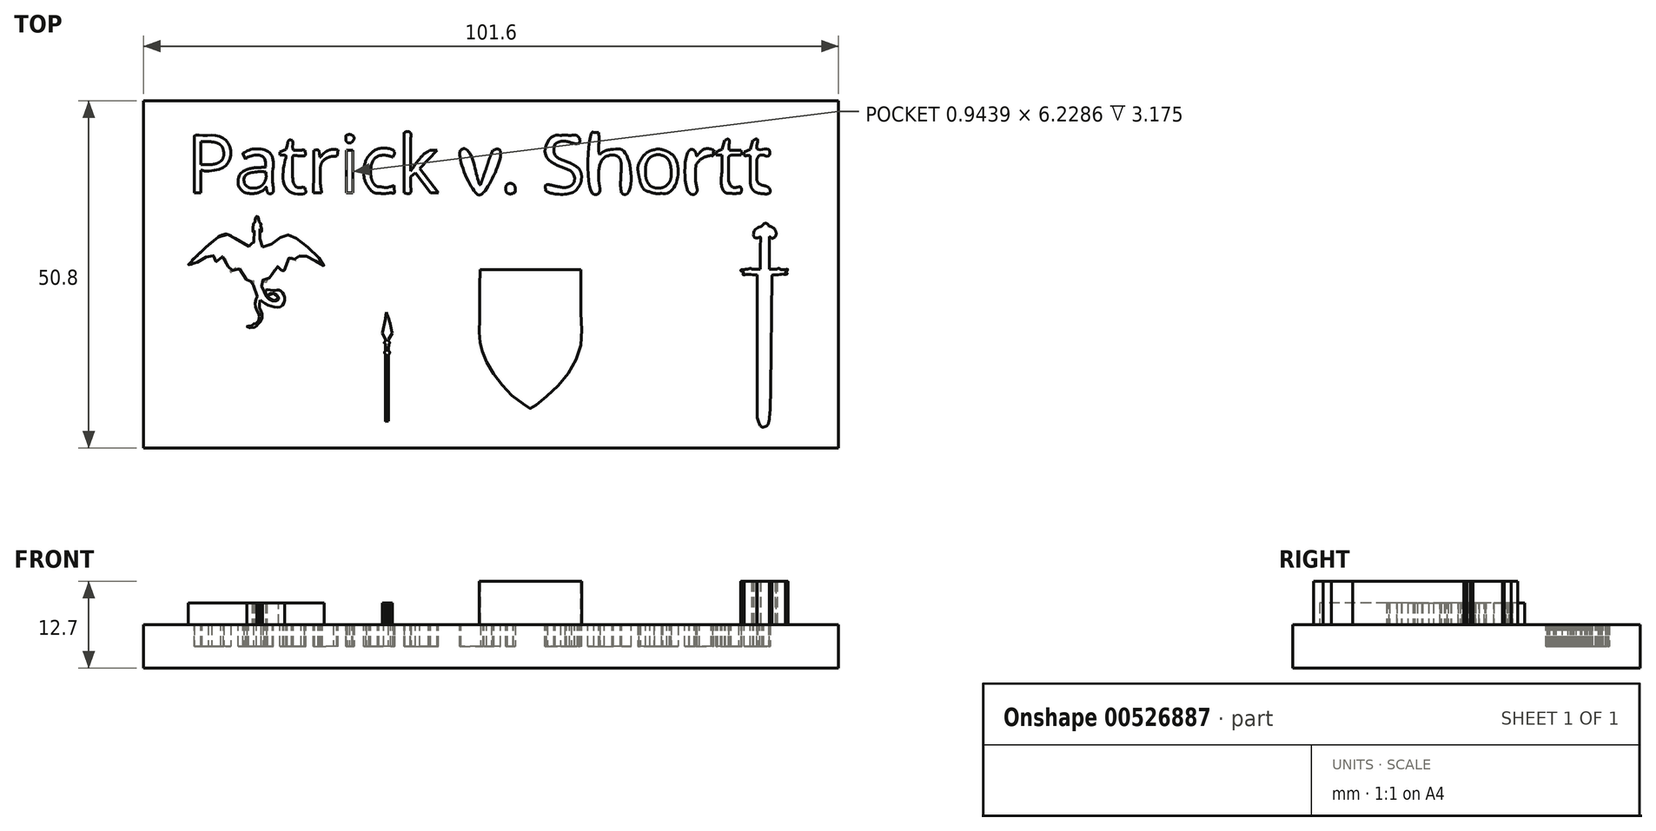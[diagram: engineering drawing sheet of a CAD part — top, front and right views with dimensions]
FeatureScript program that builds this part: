
annotation { "Feature Type Name" : "Feature", "Feature Type Description" : "" }
export const myFeature = defineFeature(function(context is Context, id is Id, definition is map)
    precondition{}
    {
        {
            var Q0;
            Q0=qCreatedBy(makeId("Top.planeOp"),FACE);
            var sketch = newSketch(context, id + "F0", { "sketchPlane" : qUnion([Q0])});
            skLineSegment(sketch, "E0.bottom", {"start": v(-59.4, 0) * mm, "end": v(42.2, 0) * mm});
            skLineSegment(sketch, "E0.top", {"start": v(-59.4, 50.8) * mm, "end": v(42.2, 50.8) * mm});
            skLineSegment(sketch, "E0.left", {"start": v(-59.4, 0) * mm, "end": v(-59.4, 50.8) * mm});
            skLineSegment(sketch, "E0.right", {"start": v(42.2, 0) * mm, "end": v(42.2, 50.8) * mm});
            skSolve(sketch);
        }
        {
            var Q0;
            Q0=makeQuery(id+"F0.imprint","IMPRINT",FACE,{"disambiguationData":[TD([[makeQuery(id+"F0.imprint","IMPRINT",EDGE,{"derivedFrom":sQuery(id+"F0.wireOp",EDGE,"E0.bottom")}),1.0]])]});
            extrude(context, id + "F1", {"entities" : qUnion([Q0]), "depth" : 6.35 * mm, "offsetDistance" : 25.4 * mm});
        }
        {
            var Q0;
            Q0=makeQuery(id+"F1.opExtrude","CAP_FACE",FACE,{"disambiguationData":[OSD([sQuery(id+"F0.wireOp",EDGE,"E0.bottom"),sQuery(id+"F0.wireOp",EDGE,"E0.top"),sQuery(id+"F0.wireOp",EDGE,"E0.left"),sQuery(id+"F0.wireOp",EDGE,"E0.right")])],"isStart":false});
            var sketch = newSketch(context, id + "F2", { "sketchPlane" : qUnion([Q0])});
            skText(sketch, "E1", { "text": "Patrick v. Shortt\n", "fontName": "OpenSans-Regular.ttf"});
            skFitSpline(sketch, "E2", {"points": [v(-51.95, 37.34) * mm, v(-51.93, 38.16) * mm, v(-51.93, 38.92) * mm, v(-51.96, 39.37) * mm, v(-51.93, 43.02) * mm, v(-51.93, 45.24) * mm, v(-51.93, 45.72) * mm, v(-50.8, 45.72) * mm, v(-48.78, 45.72) * mm, v(-47.31, 44.97) * mm, v(-46.64, 43.43) * mm, v(-47.09, 41.63) * mm, v(-48.59, 40.73) * mm, v(-50.77, 40.58) * mm, v(-51.03, 40.65) * mm, v(-50.96, 37.34) * mm], "startDerivative": vector(0.26, 16.03) * mm, "endDerivative": vector(3.57, -47.2) * mm});
            skFitSpline(sketch, "E3", {"points": [v(-51, 44.75) * mm, v(-51, 41.63) * mm], "startDerivative": vector(0, -3.12) * mm, "endDerivative": vector(0, -3.12) * mm});
            skFitSpline(sketch, "E4", {"points": [v(-51, 41.63) * mm, v(-49.11, 41.63) * mm, v(-47.84, 42.27) * mm, v(-47.76, 43.7) * mm, v(-48.33, 44.41) * mm, v(-49.38, 44.79) * mm, v(-50.43, 44.79) * mm, v(-51, 44.75) * mm], "startDerivative": vector(10.5, -0.7) * mm, "endDerivative": vector(-5.2, -0.33) * mm});
            skFitSpline(sketch, "E5", {"points": [v(-44.83, 43.06) * mm, v(-44.5, 42.23) * mm], "startDerivative": vector(0.34, -0.83) * mm, "endDerivative": vector(0.34, -0.83) * mm});
            skFitSpline(sketch, "E6", {"points": [v(-44.5, 42.23) * mm, v(-44.23, 42.5) * mm, v(-43.4, 42.79) * mm, v(-42.54, 42.85) * mm, v(-41.94, 42.62) * mm, v(-41.64, 42.14) * mm, v(-41.51, 41.11) * mm, v(-41.52, 41.07) * mm, v(-41.76, 41.06) * mm, v(-42.17, 41.05) * mm, v(-42.72, 41.03) * mm, v(-43.11, 41) * mm, v(-43.71, 40.9) * mm, v(-44.38, 40.71) * mm, v(-45.03, 40.32) * mm, v(-45.5, 39.57) * mm, v(-45.54, 38.58) * mm, v(-45.3, 38) * mm, v(-44.5, 37.34) * mm, v(-43.22, 37.34) * mm, v(-41.77, 37.8) * mm, v(-41.46, 38.2) * mm, v(-41.21, 37.34) * mm, v(-40.51, 37.34) * mm, v(-40.56, 39.3) * mm, v(-40.41, 41.85) * mm, v(-40.96, 43.2) * mm, v(-42.37, 43.76) * mm, v(-43.87, 43.6) * mm, v(-44.83, 43.06) * mm], "startDerivative": vector(8.8, 12.46) * mm, "endDerivative": vector(-22.31, -15.8) * mm});
            skFitSpline(sketch, "E7", {"points": [v(-41.67, 40.35) * mm, v(-42.92, 40.4) * mm, v(-44.5, 39.85) * mm, v(-44.5, 38.5) * mm, v(-43.02, 38.1) * mm, v(-41.92, 38.7) * mm, v(-41.46, 39.55) * mm, v(-41.67, 40.35) * mm]});
            skFitSpline(sketch, "E8", {"points": [v(-38.15, 45.01) * mm, v(-38.56, 43.66) * mm, v(-39.3, 43.26) * mm, v(-39.36, 42.9) * mm, v(-38.6, 42.8) * mm, v(-38.66, 42.2) * mm, v(-38.4, 37.84) * mm, v(-35.7, 37.34) * mm, v(-35.8, 37.9) * mm, v(-36, 38.14) * mm, v(-36.75, 38.1) * mm, v(-37.3, 38.44) * mm, v(-37.55, 39.3) * mm, v(-37.55, 42.66) * mm, v(-37.3, 42.8) * mm, v(-35.8, 42.8) * mm, v(-35.8, 43.4) * mm, v(-36.05, 43.6) * mm, v(-37.4, 43.5) * mm, v(-37.55, 44.56) * mm, v(-37.65, 44.96) * mm, v(-38.15, 45.01) * mm]});
            skFitSpline(sketch, "E9", {"points": [v(-34.4, 43.56) * mm, v(-34.6, 37.34) * mm], "startDerivative": vector(-0.2, -6.22) * mm, "endDerivative": vector(-0.2, -6.22) * mm});
            skFitSpline(sketch, "E10", {"points": [v(-34.6, 37.34) * mm, v(-33.34, 37.34) * mm], "startDerivative": vector(1.25, 0) * mm, "endDerivative": vector(1.25, 0) * mm});
            skFitSpline(sketch, "E11", {"points": [v(-34.4, 43.56) * mm, v(-33.84, 43.56) * mm, v(-33.8, 42.5) * mm, v(-32.79, 43.16) * mm, v(-31.84, 43.56) * mm, v(-31.23, 43.56) * mm, v(-31.08, 42.8) * mm, v(-31.84, 42.66) * mm, v(-33.34, 41.75) * mm, v(-33.34, 37.34) * mm], "startDerivative": vector(9.35, 3.26) * mm, "endDerivative": vector(3.7, -24.46) * mm});
            skFitSpline(sketch, "E12", {"points": [v(-29.48, 44.86) * mm, v(-29.73, 45.01) * mm, v(-29.78, 45.72) * mm, v(-29.33, 45.72) * mm, v(-28.78, 45.72) * mm, v(-28.68, 45.06) * mm, v(-29.48, 44.86) * mm]});
            skFitSpline(sketch, "E13", {"points": [v(-29.73, 43.4) * mm, v(-29.78, 37.34) * mm], "startDerivative": vector(-0.05, -6.07) * mm, "endDerivative": vector(-0.05, -6.07) * mm});
            skFitSpline(sketch, "E14", {"points": [v(-29.78, 37.34) * mm, v(-28.68, 37.34) * mm], "startDerivative": vector(1.1, 0) * mm, "endDerivative": vector(1.1, 0) * mm});
            skFitSpline(sketch, "E15", {"points": [v(-28.68, 37.34) * mm, v(-28.68, 43.4) * mm], "startDerivative": vector(0, 6.07) * mm, "endDerivative": vector(0, 6.07) * mm});
            skFitSpline(sketch, "E16", {"points": [v(-28.78, 43.46) * mm, v(-29.73, 43.4) * mm], "startDerivative": vector(-0.95, -0.05) * mm, "endDerivative": vector(-0.95, -0.05) * mm});
            skFitSpline(sketch, "E17", {"points": [v(-22.91, 42.66) * mm, v(-22.7, 43.4) * mm, v(-24.72, 43.86) * mm, v(-26.22, 43) * mm, v(-26.97, 41.8) * mm, v(-27.12, 39.55) * mm, v(-26.47, 38.14) * mm, v(-25.62, 37.34) * mm, v(-24.47, 37.34) * mm, v(-23.21, 37.34) * mm, v(-22.7, 37.34) * mm, v(-22.76, 38.14) * mm, v(-22.76, 38.34) * mm, v(-23.91, 38.1) * mm, v(-24.52, 38.2) * mm, v(-25.57, 38.34) * mm, v(-26.07, 39.95) * mm, v(-25.87, 41.7) * mm, v(-25.02, 42.55) * mm, v(-23.51, 42.7) * mm], "startDerivative": vector(11.92, 18.93) * mm, "endDerivative": vector(27.23, -0.59) * mm});
            skFitSpline(sketch, "E18", {"points": [v(-21.2, 45.72) * mm, v(-21.26, 37.34) * mm], "startDerivative": vector(-0.05, -8.38) * mm, "endDerivative": vector(-0.05, -8.38) * mm});
            skFitSpline(sketch, "E19", {"points": [v(-21.2, 45.72) * mm, v(-21.2, 46.17) * mm, v(-20.45, 46.22) * mm, v(-20.35, 45.01) * mm, v(-20.35, 40.5) * mm], "startDerivative": vector(-1.16, 3.61) * mm, "endDerivative": vector(0.35, -11.33) * mm});
            skFitSpline(sketch, "E20", {"points": [v(-20.35, 40.5) * mm, v(-17.75, 43.4) * mm, v(-16.8, 43.4) * mm, v(-16.64, 43.4) * mm, v(-18.9, 41) * mm], "startDerivative": vector(7.14, 10.37) * mm, "endDerivative": vector(-9.74, -9.77) * mm});
            skFitSpline(sketch, "E21", {"points": [v(-18.9, 41) * mm, v(-16.24, 37.34) * mm], "startDerivative": vector(2.66, -3.66) * mm, "endDerivative": vector(2.66, -3.66) * mm});
            skFitSpline(sketch, "E22", {"points": [v(-16.34, 37.29) * mm, v(-17.9, 37.34) * mm], "startDerivative": vector(-1.55, 0.05) * mm, "endDerivative": vector(-1.55, 0.05) * mm});
            skFitSpline(sketch, "E23", {"points": [v(-17.8, 37.5) * mm, v(-19.5, 40) * mm], "startDerivative": vector(-1.7, 2.5) * mm, "endDerivative": vector(-1.7, 2.5) * mm});
            skFitSpline(sketch, "E24", {"points": [v(-19.5, 40) * mm, v(-20.35, 39.55) * mm, v(-20.35, 37.34) * mm, v(-21.26, 37.34) * mm], "startDerivative": vector(-3.83, -0.46) * mm, "endDerivative": vector(-4.14, 1.32) * mm});
            skFitSpline(sketch, "E25", {"points": [v(-13.08, 43.4) * mm, v(-10.83, 37.34) * mm, v(-9.72, 37.34) * mm, v(-7.21, 43.4) * mm, v(-8.27, 43.4) * mm, v(-10.1, 38.44) * mm, v(-11.88, 43.4) * mm, v(-13.08, 43.4) * mm]});
            skFitSpline(sketch, "E26", {"points": [v(-6.06, 38.6) * mm, v(-5.71, 38.64) * mm, v(-5.3, 38.6) * mm, v(-5.06, 38.1) * mm, v(-5.1, 37.34) * mm, v(-5.3, 37.34) * mm, v(-5.61, 37.34) * mm, v(-5.91, 37.34) * mm, v(-6.26, 37.34) * mm, v(-6.36, 38) * mm, v(-6.06, 38.6) * mm]});
            skFitSpline(sketch, "E27", {"points": [v(4.18, 44.53) * mm, v(4.4, 45.06) * mm, v(3.97, 45.72) * mm, v(2.9, 45.72) * mm, v(1.68, 45.72) * mm, v(0.67, 45.72) * mm, v(-0.5, 44.37) * mm, v(-0.5, 42.62) * mm, v(1.26, 41.3) * mm, v(3.22, 40.39) * mm, v(3.6, 38.95) * mm, v(2.27, 38.1) * mm, v(-0.55, 38.48) * mm, v(-0.55, 37.78) * mm, v(0, 37.34) * mm, v(3.22, 37.34) * mm, v(4.55, 38.95) * mm, v(4.55, 40.39) * mm, v(3.86, 41.18) * mm, v(1.9, 42.14) * mm, v(0.73, 42.94) * mm, v(0.83, 44.48) * mm, v(2.21, 44.9) * mm, v(4.18, 44.53) * mm]});
            skFitSpline(sketch, "E28", {"points": [v(6.25, 46.23) * mm, v(6.2, 37.34) * mm, v(7.2, 37.34) * mm, v(7.2, 38.9) * mm, v(7.31, 41.34) * mm, v(8.11, 42.57) * mm, v(9.54, 42.88) * mm, v(10.4, 42.25) * mm, v(10.55, 37.34) * mm, v(11.46, 37.34) * mm, v(11.3, 42.73) * mm, v(9.39, 43.68) * mm, v(7.31, 43) * mm, v(7.2, 45.72) * mm, v(6.94, 45.72) * mm, v(6.25, 46.23) * mm]});
            skFitSpline(sketch, "E29", {"points": [v(15.28, 43.63) * mm, v(16.5, 43.63) * mm, v(17.78, 43.04) * mm, v(18.58, 41.88) * mm, v(18.58, 39.06) * mm, v(17.3, 37.34) * mm, v(15.65, 37.34) * mm, v(13.8, 37.84) * mm, v(13.05, 39.75) * mm, v(13.05, 41.66) * mm, v(15.28, 43.63) * mm]});
            skFitSpline(sketch, "E30", {"points": [v(16.56, 42.73) * mm, v(15.18, 42.78) * mm, v(14.49, 41.98) * mm, v(14.17, 39.96) * mm, v(14.7, 38.69) * mm, v(15.81, 38.1) * mm, v(17.3, 38.63) * mm, v(17.73, 40.39) * mm, v(16.56, 42.73) * mm]});
            skFitSpline(sketch, "E31", {"points": [v(20.33, 43.47) * mm, v(20.38, 37.34) * mm, v(21.45, 37.34) * mm, v(21.34, 39) * mm, v(21.66, 41.82) * mm, v(23.52, 42.78) * mm, v(23.94, 42.83) * mm, v(23.89, 43.3) * mm, v(23.89, 43.58) * mm, v(22.35, 43.63) * mm, v(21.55, 42.62) * mm, v(21.23, 43.42) * mm, v(20.33, 43.47) * mm]});
            skFitSpline(sketch, "E32", {"points": [v(26.23, 45.06) * mm, v(25.8, 45.12) * mm, v(25.32, 43.79) * mm, v(24.63, 43.47) * mm, v(24.42, 43.1) * mm, v(25.16, 42.94) * mm, v(25.06, 39.17) * mm, v(25.8, 37.34) * mm, v(27.34, 37.34) * mm, v(27.93, 37.34) * mm, v(27.93, 38.16) * mm, v(27.18, 38.1) * mm, v(26.33, 38.63) * mm, v(26.23, 42.67) * mm, v(27.77, 42.88) * mm, v(28.09, 43.3) * mm, v(26.33, 43.52) * mm, v(26.23, 45.06) * mm]});
            skFitSpline(sketch, "E33", {"points": [v(29.9, 45.06) * mm, v(30.37, 45.12) * mm, v(30.37, 43.73) * mm, v(32.02, 43.68) * mm, v(31.96, 42.73) * mm, v(30.69, 42.83) * mm, v(30.42, 38.9) * mm, v(31.86, 38.2) * mm, v(32.18, 37.34) * mm, v(30.53, 37.34) * mm, v(29.52, 38.26) * mm, v(29.3, 42.73) * mm, v(28.51, 42.78) * mm, v(28.56, 43.3) * mm, v(29.36, 43.73) * mm, v(29.9, 45.06) * mm]});
            const initialGuessF2  = {"E1": [-0.05309, 0.03734, 1, 0, 0.00838]};
            skSetInitialGuess(sketch, initialGuessF2);
            skSolve(sketch);
        }
        {
            var Q0;
            Q0=makeQuery(id+"F2.imprint","IMPRINT",FACE,{"disambiguationData":[TD([[makeQuery(id+"F2.imprint","IMPRINT",EDGE,{"derivedFrom":sQuery(id+"F2.wireOp",EDGE,"E1.sketch_text.stroke-0")}),1.0]])]});
            var sketch = newSketch(context, id + "F3", { "sketchPlane" : qUnion([Q0])});
            skFitSpline(sketch, "E34", {"points": [v(-43.36, 32.77) * mm, v(-43.2, 32.9) * mm, v(-43.08, 33.06) * mm, v(-43.05, 33.4) * mm, v(-42.98, 33.71) * mm, v(-42.92, 33.8) * mm, v(-42.81, 33.91) * mm, v(-42.63, 33.76) * mm, v(-42.5, 33.12) * mm, v(-42.24, 32.83) * mm, v(-42.17, 32.71) * mm, v(-42.26, 32.68) * mm, v(-42.25, 32.35) * mm, v(-42.16, 32.19) * mm, v(-42.12, 31.62) * mm, v(-42.24, 31.79) * mm, v(-42.3, 32.1) * mm, v(-42.4, 32.07) * mm], "startDerivative": vector(2.94, 2.65) * mm, "endDerivative": vector(-3.17, -1.64) * mm});
            skLineSegment(sketch, "E35", {"start": v(-42.36, 32.1) * mm, "end": v(-42.36, 30.6) * mm});
            skLineSegment(sketch, "E36", {"start": v(-42.36, 30.6) * mm, "end": v(-42, 29.4) * mm});
            skFitSpline(sketch, "E37", {"points": [v(-43.36, 32.77) * mm, v(-43.36, 32.67) * mm, v(-43.29, 32.6) * mm, v(-43.36, 32.24) * mm, v(-43.48, 31.72) * mm, v(-43.43, 31.58) * mm, v(-43.29, 31.98) * mm, v(-43.22, 32.02) * mm, v(-43.2, 31.94) * mm, v(-43.25, 30.47) * mm, v(-43.52, 29.4) * mm, v(-45.95, 30.66) * mm, v(-46.89, 31.17) * mm, v(-47.66, 31.26) * mm, v(-49.97, 29.62) * mm, v(-51.9, 27.82) * mm, v(-52.84, 26.77) * mm, v(-51.42, 27.19) * mm, v(-50.29, 27.9) * mm, v(-49.34, 28.2) * mm, v(-48.98, 27.9) * mm, v(-48.8, 27.25) * mm, v(-48.08, 27.84) * mm, v(-47.55, 27.9) * mm, v(-46.6, 25.64) * mm, v(-46.11, 26.35) * mm, v(-45.34, 26.17) * mm, v(-44.27, 24.44) * mm, v(-44.2, 24.2) * mm, v(-43.36, 24.5) * mm, v(-43.36, 23.79) * mm, v(-42.63, 22) * mm, v(-40.93, 20.8) * mm, v(-39.14, 20.8) * mm, v(-38.84, 22.3) * mm, v(-39.56, 23.07) * mm, v(-40.4, 23.07) * mm, v(-41.46, 23.13) * mm, v(-41.52, 22.72) * mm], "startDerivative": vector(-2.57, -12.43) * mm, "endDerivative": vector(4.15, -29.38) * mm});
            skFitSpline(sketch, "E38", {"points": [v(-42.75, 22.16) * mm, v(-42.83, 22) * mm, v(-43.04, 21.3) * mm, v(-43.01, 20.67) * mm, v(-42.85, 20.26) * mm, v(-42.62, 19.76) * mm, v(-42.47, 19.42) * mm, v(-42.49, 18.78) * mm, v(-42.91, 18.24) * mm, v(-43.15, 18.23) * mm, v(-43.3, 18.1) * mm, v(-43.6, 17.89) * mm, v(-44, 17.81) * mm, v(-44.2, 17.81) * mm, v(-44.26, 17.76) * mm, v(-44.1, 17.64) * mm, v(-43.3, 17.64) * mm, v(-42.86, 17.81) * mm, v(-42.84, 17.95) * mm, v(-42.66, 18.17) * mm, v(-42.32, 18.47) * mm, v(-42.03, 19.07) * mm, v(-42.07, 19.74) * mm, v(-42.32, 20.23) * mm, v(-42.46, 20.53) * mm, v(-42.43, 21.06) * mm, v(-42.36, 21.54) * mm], "startDerivative": vector(-2.97, -4.68) * mm, "endDerivative": vector(1.81, 10.93) * mm});
            skFitSpline(sketch, "E39", {"points": [v(-42, 29.4) * mm, v(-41.65, 29.4) * mm, v(-40.4, 30.03) * mm, v(-39.62, 30.63) * mm, v(-38.66, 31.16) * mm, v(-38.33, 31.2) * mm, v(-38.03, 31.22) * mm, v(-37.1, 30.72) * mm, v(-35.57, 29.55) * mm, v(-33.98, 28.05) * mm, v(-32.97, 26.9) * mm, v(-33, 26.7) * mm, v(-33.37, 26.83) * mm, v(-34.47, 27.47) * mm, v(-35.35, 27.95) * mm, v(-36, 28.22) * mm, v(-36.55, 28.25) * mm, v(-36.92, 27.23) * mm, v(-37.36, 27.73) * mm, v(-37.75, 27.97) * mm, v(-38.03, 27.9) * mm, v(-38.72, 26.4) * mm, v(-38.93, 25.65) * mm, v(-38.98, 25.59) * mm, v(-39.15, 25.92) * mm, v(-39.36, 26.2) * mm, v(-39.61, 26.45) * mm, v(-39.76, 26.54) * mm, v(-39.98, 26.56) * mm, v(-41.46, 24.22) * mm, v(-41.77, 24.44) * mm, v(-42, 24.67) * mm, v(-42.07, 24.73) * mm, v(-42.07, 23.32) * mm, v(-41.52, 22.3) * mm, v(-40.7, 21.58) * mm, v(-40.13, 21.54) * mm, v(-39.85, 21.6) * mm, v(-39.63, 21.93) * mm, v(-39.84, 22.3) * mm, v(-40.04, 22.53) * mm, v(-40.51, 22.6) * mm, v(-40.88, 22.6) * mm, v(-41.34, 22.3) * mm], "startDerivative": vector(16.86, -3.32) * mm, "endDerivative": vector(-22.38, -17.65) * mm});
            skLineSegment(sketch, "E40", {"start": v(-41.52, 22.72) * mm, "end": v(-41.34, 22.3) * mm});
            skLineSegment(sketch, "E41", {"start": v(-42.34, 21.68) * mm, "end": v(-42.36, 21.54) * mm});
            skSolve(sketch);
        }
        {
            var Q0;
            Q0=makeQuery(id+"F3.imprint","IMPRINT",FACE,{"disambiguationData":[TD([[makeQuery(id+"F3.imprint","IMPRINT",EDGE,{"derivedFrom":makeQuery(id+"F2.imprint","IMPRINT",EDGE,{"derivedFrom":sQuery(id+"F2.wireOp",EDGE,"E1.sketch_text.stroke-0")})}),1.0]])]});
            var sketch = newSketch(context, id + "F4", { "sketchPlane" : qUnion([Q0])});
            skPoint(sketch, "E42.4.internal.snap0", {"position": v(31.37, 32.87) * mm});
            skFitSpline(sketch, "E42", {"points": [v(31.1, 32.56) * mm, v(31.17, 32.68) * mm, v(31.2, 32.7) * mm, v(31.27, 32.77) * mm, v(31.37, 32.83) * mm, v(31.48, 32.87) * mm, v(31.67, 32.87) * mm, v(31.85, 32.77) * mm, v(31.96, 32.62) * mm, v(31.99, 32.51) * mm, v(32.06, 32.45) * mm, v(32.18, 32.44) * mm, v(32.36, 32.37) * mm, v(32.51, 32.3) * mm, v(32.6, 32.24) * mm, v(32.71, 32.2) * mm, v(32.8, 32.12) * mm, v(32.94, 31.95) * mm], "startDerivative": vector(1.28, 2.48) * mm, "endDerivative": vector(2.04, -2.4) * mm});
            skFitSpline(sketch, "E43", {"points": [v(32.94, 31.95) * mm, v(32.99, 31.85) * mm, v(33.05, 31.7) * mm, v(33.08, 31.6) * mm, v(33.1, 31.44) * mm, v(33.1, 31.33) * mm, v(33.08, 31.17) * mm, v(33.02, 31.05) * mm, v(32.9, 30.88) * mm, v(32.73, 30.74) * mm, v(32.61, 30.7) * mm, v(32.5, 30.69) * mm, v(32.4, 30.7) * mm, v(32.3, 30.77) * mm, v(32.18, 30.9) * mm, v(32.14, 30.9) * mm, v(32.12, 30.86) * mm, v(32.1, 30.78) * mm, v(32.1, 30.7) * mm], "startDerivative": vector(0.92, -1.63) * mm, "endDerivative": vector(0.06, -1.73) * mm});
            skFitSpline(sketch, "E44", {"points": [v(31.1, 32.56) * mm, v(31.05, 32.48) * mm, v(30.91, 32.42) * mm, v(30.74, 32.39) * mm, v(30.54, 32.32) * mm, v(30.38, 32.24) * mm, v(30.22, 32.12) * mm, v(30.08, 32) * mm, v(30, 31.94) * mm, v(29.9, 31.78) * mm, v(29.84, 31.62) * mm, v(29.8, 31.42) * mm, v(29.8, 31.3) * mm, v(29.8, 31.23) * mm, v(29.84, 31.02) * mm, v(29.97, 30.83) * mm, v(30.16, 30.7) * mm, v(30.37, 30.7) * mm, v(30.56, 30.79) * mm, v(30.7, 30.9) * mm, v(30.8, 30.9) * mm, v(30.82, 30.7) * mm, v(30.76, 26.14) * mm], "startDerivative": vector(-1.56, -2.98) * mm, "endDerivative": vector(-0.26, -30.28) * mm});
            skLineSegment(sketch, "E45", {"start": v(30.76, 26.14) * mm, "end": v(29.54, 26.14) * mm});
            skFitSpline(sketch, "E46", {"points": [v(29.54, 26.14) * mm, v(29.5, 26.14) * mm], "startDerivative": vector(-0.03, 0) * mm, "endDerivative": vector(-0.03, 0) * mm});
            skFitSpline(sketch, "E47", {"points": [v(29.52, 26.14) * mm, v(29.5, 26.16) * mm, v(29.49, 26.2) * mm, v(29.43, 26.28) * mm, v(29.38, 26.32) * mm, v(29.3, 26.32) * mm, v(29.2, 26.24) * mm, v(29.06, 26.19) * mm, v(28.92, 26.17) * mm, v(28.72, 26.17) * mm, v(28.58, 26.16) * mm, v(28.53, 26.14) * mm, v(28.43, 26.08) * mm, v(28.29, 26.1) * mm, v(28.2, 26.11) * mm, v(28.05, 26.11) * mm, v(27.99, 26.08) * mm, v(27.95, 26.03) * mm, v(27.95, 25.95) * mm, v(28, 25.89) * mm, v(28.07, 25.84) * mm, v(28.1, 25.84) * mm, v(28.41, 25.6) * mm, v(28.37, 25.56) * mm, v(28.26, 25.5) * mm, v(28.22, 25.47) * mm, v(28.2, 25.42) * mm, v(28.24, 25.34) * mm, v(28.3, 25.3) * mm, v(28.44, 25.31) * mm, v(28.57, 25.33) * mm, v(28.71, 25.37) * mm, v(28.81, 25.4) * mm, v(28.92, 25.42) * mm, v(29.1, 25.42) * mm, v(29.25, 25.4) * mm, v(29.46, 25.38) * mm, v(29.73, 25.36) * mm, v(30.03, 25.35) * mm, v(30.27, 25.34) * mm], "startDerivative": vector(-1.4, 1.41) * mm, "endDerivative": vector(6.24, -0.3) * mm});
            skLineSegment(sketch, "E48", {"start": v(32.1, 30.7) * mm, "end": v(32.1, 26.17) * mm});
            skLineSegment(sketch, "E49", {"start": v(32.1, 26.17) * mm, "end": v(33.23, 26.17) * mm});
            skPoint(sketch, "E50.9.internal.snap0", {"position": v(32.67, 26.17) * mm});
            skPoint(sketch, "E50.10.internal.snap0", {"position": v(32.67, 26.17) * mm});
            skPoint(sketch, "E50.11.internal.snap0", {"position": v(32.67, 26.17) * mm});
            skFitSpline(sketch, "E50", {"points": [v(33.23, 26.17) * mm, v(33.3, 26.2) * mm, v(33.38, 26.29) * mm, v(33.45, 26.32) * mm, v(33.55, 26.3) * mm, v(33.75, 26.08) * mm, v(33.82, 26.08) * mm, v(34.12, 26.08) * mm, v(34.34, 26.08) * mm, v(34.57, 26.17) * mm, v(34.72, 26.17) * mm, v(34.8, 26.17) * mm, v(34.8, 26) * mm, v(34.75, 25.98) * mm, v(34.6, 25.84) * mm, v(34.45, 25.7) * mm, v(34.5, 25.66) * mm, v(34.56, 25.65) * mm, v(34.63, 25.63) * mm, v(34.68, 25.6) * mm, v(34.73, 25.56) * mm, v(34.72, 25.5) * mm, v(34.65, 25.46) * mm, v(34.57, 25.43) * mm, v(34.45, 25.42) * mm, v(34.35, 25.41) * mm, v(34.18, 25.42) * mm, v(34.03, 25.44) * mm, v(33.92, 25.44) * mm, v(33.8, 25.41) * mm, v(33.76, 25.4) * mm, v(33.7, 25.38) * mm, v(33.54, 25.38) * mm, v(33.28, 25.36) * mm, v(33.13, 25.36) * mm, v(33, 25.36) * mm, v(32.87, 25.36) * mm, v(32.72, 25.34) * mm, v(32.58, 25.34) * mm, v(32.54, 25.29) * mm, v(32.5, 25.18) * mm, v(32.5, 25.03) * mm], "startDerivative": vector(3.66, 1.71) * mm, "endDerivative": vector(0.06, -5.67) * mm});
            skLineSegment(sketch, "E51", {"start": v(32.5, 25.03) * mm, "end": v(32.3, 8.78) * mm});
            skLineSegment(sketch, "E52", {"start": v(32.3, 8.78) * mm, "end": v(32.22, 5.65) * mm});
            skLineSegment(sketch, "E53", {"start": v(32.22, 5.65) * mm, "end": v(32.13, 4.42) * mm});
            skLineSegment(sketch, "E54", {"start": v(30.27, 25.34) * mm, "end": v(30.33, 25.34) * mm});
            skLineSegment(sketch, "E55", {"start": v(30.33, 25.34) * mm, "end": v(30.33, 24.78) * mm});
            skLineSegment(sketch, "E56", {"start": v(30.33, 24.78) * mm, "end": v(30.33, 23.4) * mm});
            skLineSegment(sketch, "E57", {"start": v(30.33, 23.4) * mm, "end": v(30.33, 21.45) * mm});
            skLineSegment(sketch, "E58", {"start": v(30.33, 21.45) * mm, "end": v(30.33, 4.42) * mm});
            skFitSpline(sketch, "E59", {"points": [v(30.33, 4.42) * mm, v(30.7, 3.42) * mm, v(31.06, 3.07) * mm, v(31.78, 3.32) * mm, v(32.03, 3.82) * mm, v(32.13, 4.42) * mm], "startDerivative": vector(1.45, -4.4) * mm, "endDerivative": vector(0.47, 3.23) * mm});
            skLineSegment(sketch, "E60", {"start": v(-10.2, 26.07) * mm, "end": v(4.57, 26.07) * mm});
            skPoint(sketch, "E61.7.internal.snap0", {"position": v(-2.76, 4.97) * mm});
            skFitSpline(sketch, "E61", {"points": [v(4.57, 26.07) * mm, v(4.57, 23.69) * mm, v(4.57, 19.33) * mm, v(4.57, 15.19) * mm, v(3.17, 11.7) * mm, v(0.65, 8.52) * mm, v(-1.94, 6.34) * mm, v(-2.76, 5.78) * mm, v(-3.26, 6.03) * mm, v(-5.27, 7.47) * mm, v(-7.5, 9.9) * mm, v(-9.17, 12.44) * mm, v(-9.93, 14.45) * mm, v(-10.25, 15.72) * mm, v(-10.25, 17.9) * mm, v(-10.25, 21.58) * mm, v(-10.2, 26.07) * mm], "startDerivative": vector(0.28, -37.57) * mm, "endDerivative": vector(0.97, 56.86) * mm});
            skSolve(sketch);
        }
        {
            var Q0;
            Q0 = qSketchRegion(id + "F2", true);
            extrude(context, id + "F5", {"entities" : qUnion([Q0]), "operationType" : NewBodyOperationType.REMOVE, "oppositeDirection" : true, "depth" : 3.17 * mm, "offsetDistance" : 25.4 * mm});
        }
        {
            var Q0;
            Q0 = qSketchRegion(id + "F4", true);
            var Q1;
            {var subQ4=sQuery(id+"F3.wireOp",EDGE,"E36");Q1=makeQuery(id+"F3.imprint","IMPRINT",FACE,{"disambiguationData":[TD([[makeQuery(id+"F3.imprint","IMPRINT",EDGE,{"derivedFrom":subQ4}),-1.0]])]});}
            var Q2;
            {var subQ0=sQuery(id+"F3.wireOp",EDGE,"E38");Q2=makeQuery(id+"F3.imprint","IMPRINT",FACE,{"disambiguationData":[TD([[makeQuery(id+"F3.imprint","IMPRINT",EDGE,{"derivedFrom":subQ0}),1.0]])]});}
            extrude(context, id + "F6", {"entities" : qUnion([Q0, Q1, Q2]), "operationType" : NewBodyOperationType.ADD, "depth" : 3.17 * mm, "offsetDistance" : 25.4 * mm});
        }
        {
            var Q0;
            {var subQ109=sQuery(id+"F0.wireOp",EDGE,"E0.left");var subQ114=sQuery(id+"F0.wireOp",EDGE,"E0.top");var subQ120=sQuery(id+"F0.wireOp",EDGE,"E0.bottom");var subQ146=sQuery(id+"F0.wireOp",EDGE,"E0.right");Q0=makeQuery(id+"F5.boolean.opBoolean","SPLIT",FACE,{"disambiguationData":[TD([makeQuery(id+"F1.opExtrude","SWEPT_FACE",FACE,{"disambiguationData":[OSD([subQ120])]})])],"derivedFrom":makeQuery(id+"F1.opExtrude","CAP_FACE",FACE,{"disambiguationData":[OSD([subQ120,subQ114,subQ109,subQ146])],"isStart":false})});}
            var sketch = newSketch(context, id + "F7", { "sketchPlane" : qUnion([Q0])});
            skFitSpline(sketch, "E62", {"points": [v(-24.48, 16.8) * mm, v(-24.05, 18.84) * mm], "startDerivative": vector(0.43, 2.04) * mm, "endDerivative": vector(0.43, 2.04) * mm});
            skFitSpline(sketch, "E63", {"points": [v(-24.05, 18.97) * mm, v(-23.88, 19.87) * mm], "startDerivative": vector(0.17, 0.9) * mm, "endDerivative": vector(0.17, 0.9) * mm});
            skFitSpline(sketch, "E64", {"points": [v(-23.88, 19.87) * mm, v(-23.5, 18.84) * mm, v(-23.03, 16.83) * mm], "startDerivative": vector(0.9, -2.23) * mm, "endDerivative": vector(0.8, -3.78) * mm});
            skFitSpline(sketch, "E65", {"points": [v(-23.03, 16.83) * mm, v(-23.55, 15.89) * mm], "startDerivative": vector(-0.52, -0.94) * mm, "endDerivative": vector(-0.52, -0.94) * mm});
            skFitSpline(sketch, "E66", {"points": [v(-24.48, 16.8) * mm, v(-24.05, 15.9) * mm], "startDerivative": vector(0.43, -0.9) * mm, "endDerivative": vector(0.43, -0.9) * mm});
            skFitSpline(sketch, "E67", {"points": [v(-24.05, 15.9) * mm, v(-24.05, 15.62) * mm, v(-24.2, 15.4) * mm, v(-24.05, 15.25) * mm], "startDerivative": vector(0.19, -0.84) * mm, "endDerivative": vector(0.74, -0.51) * mm});
            skFitSpline(sketch, "E68", {"points": [v(-24.05, 15.25) * mm, v(-24.05, 14.13) * mm], "startDerivative": vector(0, -1.12) * mm, "endDerivative": vector(0, -1.12) * mm});
            skFitSpline(sketch, "E69", {"points": [v(-24.05, 14.13) * mm, v(-24.18, 14) * mm, v(-24.05, 13.75) * mm], "startDerivative": vector(-0.41, -0.26) * mm, "endDerivative": vector(0.39, -0.48) * mm});
            skFitSpline(sketch, "E70", {"points": [v(-23.55, 15.89) * mm, v(-23.55, 15.62) * mm, v(-23.44, 15.52) * mm, v(-23.44, 15.25) * mm, v(-23.55, 15.25) * mm], "startDerivative": vector(-0.17, -1.1) * mm, "endDerivative": vector(-0.67, 0.23) * mm});
            skFitSpline(sketch, "E71", {"points": [v(-23.51, 15.23) * mm, v(-23.51, 14.1) * mm, v(-23.43, 14.09) * mm, v(-23.43, 13.84) * mm, v(-23.51, 13.74) * mm, v(-23.58, 13.69) * mm], "startDerivative": vector(-0.33, -3.82) * mm, "endDerivative": vector(-0.54, -0.48) * mm});
            skLineSegment(sketch, "E72", {"start": v(-24.05, 13.75) * mm, "end": v(-24.05, 3.9) * mm});
            skLineSegment(sketch, "E73", {"start": v(-24.05, 18.97) * mm, "end": v(-24.05, 18.84) * mm});
            skLineSegment(sketch, "E74", {"start": v(-23.51, 15.23) * mm, "end": v(-23.51, 15.23) * mm});
            skPoint(sketch, "E75.1.internal.orphan", {"position": v(-23.56, 3.93) * mm});
            skLineSegment(sketch, "E76", {"start": v(-23.56, 13.7) * mm, "end": v(-23.56, 3.93) * mm});
            skLineSegment(sketch, "E77", {"start": v(-24.05, 3.9) * mm, "end": v(-23.56, 3.93) * mm});
            skSolve(sketch);
        }
        {
            var Q0;
            Q0 = qSketchRegion(id + "F4", true);
            extrude(context, id + "F8", {"entities" : qUnion([Q0]), "operationType" : NewBodyOperationType.ADD, "depth" : 6.35 * mm, "offsetDistance" : 25.4 * mm});
        }
        {
            var Q0;
            Q0 = qSketchRegion(id + "F7", true);
            extrude(context, id + "F9", {"entities" : qUnion([Q0]), "operationType" : NewBodyOperationType.ADD, "depth" : 3.17 * mm, "offsetDistance" : 25.4 * mm});
        }
    });
